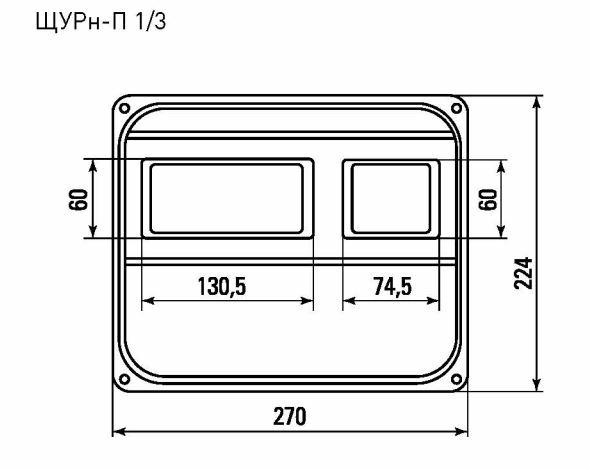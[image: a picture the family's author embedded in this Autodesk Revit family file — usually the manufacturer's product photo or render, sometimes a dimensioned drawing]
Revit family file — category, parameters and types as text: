
# Revit family: EKF_EE_ЩУРн-П_IP55_Basic
name_source: partatom
category: Электрооборудование
units: mm (PartAtom-declared; Revit-internal decimal feet)

## family parameters
Всегда вертикально = Да
На основе рабочей плоскости = Нет
Общий = Нет
При загрузке вырезать с полостями = Нет
Размер круглого соединителя = Использовать диаметр
Тип детали = Силовой щит
Точка расчета площади = Да

## types (4) — shared parameters
ADSK_Единица измерения = компл.
ADSK_Завод-изготовитель = EKF
ADSK_Классификация нагрузок = Прочее
ADSK_Количество = 1
ADSK_Количество фаз = 1
ADSK_Коэффициент мощности = 1
ADSK_Материал = Белый_ABS-пластик
ADSK_Напряжение = 400 В
ADSK_Номинальная мощность = 0 Вт
ADSK_Полная мощность = 0 В·А
ADSK_Ток = 125 А
Изготовитель = EKF
Серия номенклатуры = Basic
Степень защиты IP = IP55
ТВ = EKF
Тип установки = Навесной
zero-valued in all types: ADSK_Масса

## per-type parameters (varying)
| type | ADSK_Код изделия | ADSK_Марка | ADSK_Обозначение | ADSK_Размер_Высота | ADSK_Размер_Глубина | ADSK_Размер_Ширина | Количество DIN-реек | Количество модулей на DIN-рейке | Максимальное количество модулей | Тип |
| ЩУРн-П 1/8 (366х200х117) IP55 EKF Basic | pb-1/8-55-bas | ЩУРн-П 1/8 IP55 | ЩУРн-П 1/8 IP55 | 366 мм | 117 мм | 214 мм | 1 | 8 | 8 | 1 мм |
| ЩУРн-П 1/3 (224х270х110) IP55 EKF Basic | pb-1/3-55-bas | ЩУРн-П 1/3 IP55 | ЩУРн-П 1/3 IP55 | 224 мм | 110 мм | 270 мм | 1 | 3 | 3 | 2 мм |
| ЩУРн-П 3/10 (344х271х113) IP55 EKF Basic | pb-3/10-55-bas | ЩУРн-П 3/10 IP55 | ЩУРн-П 3/10 IP55 | 344 мм | 113 мм | 271 мм | 1 | 10 | 10 | 3 мм |
| ЩУРн-П 3/7 с КМПН (370х325х105) IP55 EKF Basic | pb-3/7-55-bas | ЩУРн-П 3/7 с КМПН IP55 | ЩУРн-П 3/7 с КМПН IP55 | 398 мм | 132 мм | 353 мм | 2 | 7 | 7 | 4 мм |

note: column(s) folded — value = type name in every type: ADSK_Наименование
